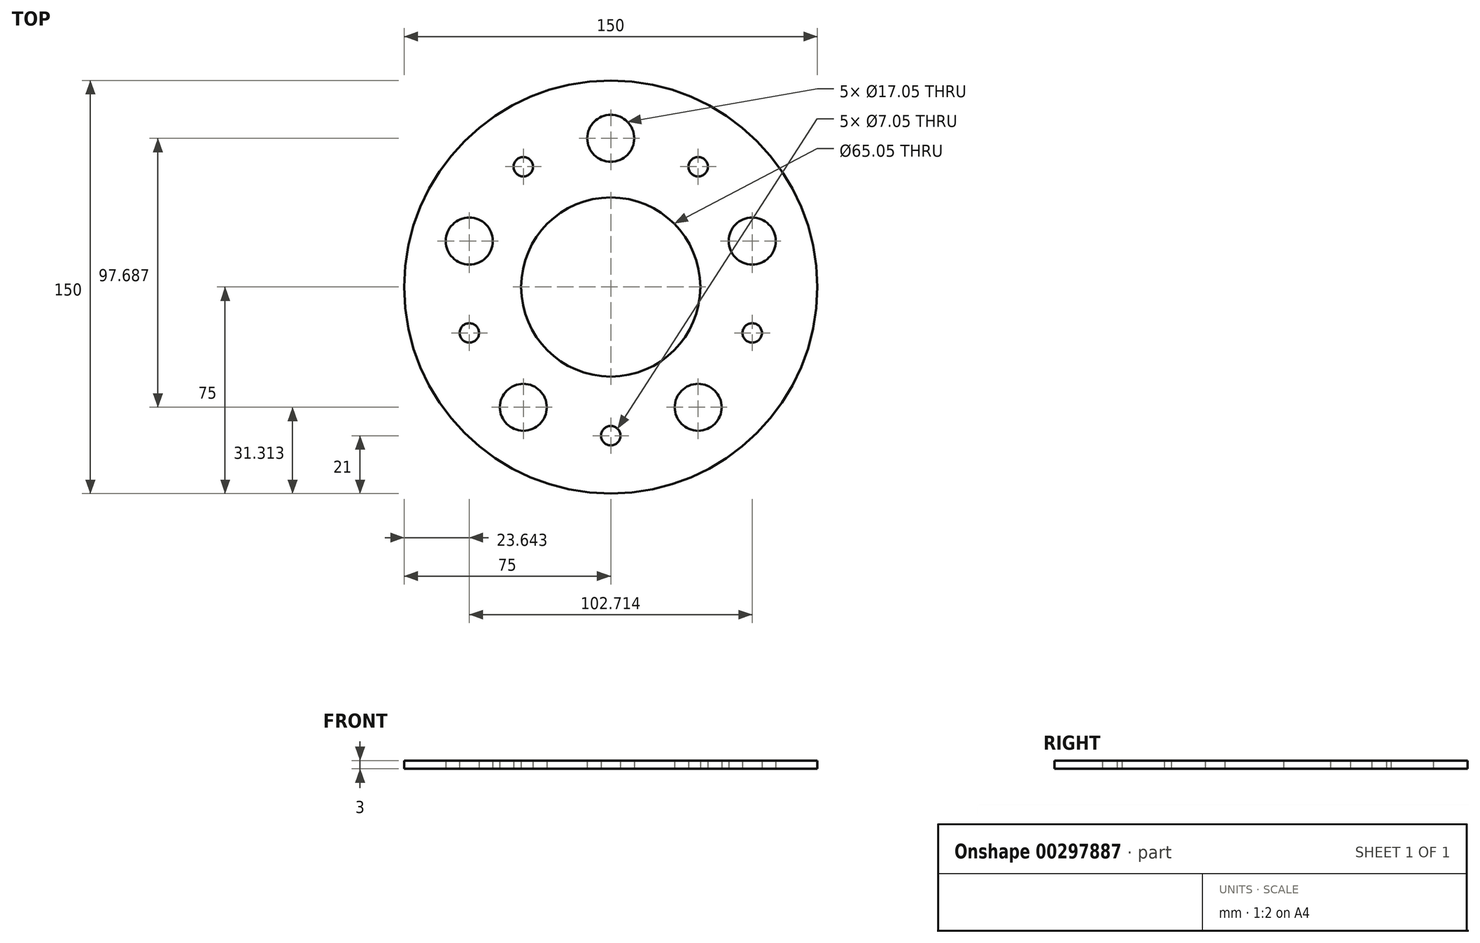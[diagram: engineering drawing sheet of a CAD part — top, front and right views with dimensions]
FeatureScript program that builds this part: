
annotation { "Feature Type Name" : "Feature", "Feature Type Description" : "" }
export const myFeature = defineFeature(function(context is Context, id is Id, definition is map)
    precondition{}
    {
        {
            var Q0;
            Q0=qCreatedBy(makeId("Top.planeOp"),FACE);
            var sketch = newSketch(context, id + "F0", { "sketchPlane" : qUnion([Q0])});
            skCircle(sketch, "E0", {"center": v(0, 0) * mm, "radius": 32.52 * mm});
            skCircle(sketch, "E1", {"center": v(0, 0) * mm, "radius": 75 * mm});
            skCircle(sketch, "E2", {"center": v(0, 0) * mm, "radius": 54 * mm, "construction": true});
            skCircle(sketch, "E3", {"center": v(0, 54) * mm, "radius": 8.53 * mm});
            skLineSegment(sketch, "E4", {"start": v(0, 54) * mm, "end": v(0, 0) * mm, "construction": true});
            skCircle(sketch, "E5.1.0", {"center": v(-51.36, 16.69) * mm, "radius": 8.53 * mm});
            skCircle(sketch, "E5.2.0", {"center": v(-31.74, -43.69) * mm, "radius": 8.53 * mm});
            skCircle(sketch, "E5.3.0", {"center": v(31.74, -43.69) * mm, "radius": 8.53 * mm});
            skCircle(sketch, "E5.4.0", {"center": v(51.36, 16.69) * mm, "radius": 8.53 * mm});
            skCircle(sketch, "E6", {"center": v(0, -54) * mm, "radius": 3.53 * mm});
            skLineSegment(sketch, "E7", {"start": v(0, 0) * mm, "end": v(0, -54) * mm, "construction": true});
            skCircle(sketch, "E8.1.0", {"center": v(51.36, -16.69) * mm, "radius": 3.53 * mm});
            skCircle(sketch, "E8.2.0", {"center": v(31.74, 43.69) * mm, "radius": 3.53 * mm});
            skCircle(sketch, "E8.3.0", {"center": v(-31.74, 43.69) * mm, "radius": 3.53 * mm});
            skCircle(sketch, "E8.4.0", {"center": v(-51.36, -16.69) * mm, "radius": 3.53 * mm});
            skSolve(sketch);
        }
        {
            var Q0;
            Q0=makeQuery(id+"F0.imprint","IMPRINT",FACE,{"disambiguationData":[TD([[makeQuery(id+"F0.imprint","IMPRINT",EDGE,{"derivedFrom":sQuery(id+"F0.wireOp",EDGE,"E0")}),-1.0]])]});
            extrude(context, id + "F1", {"entities" : qUnion([Q0]), "depth" : 3 * mm});
        }
    });
